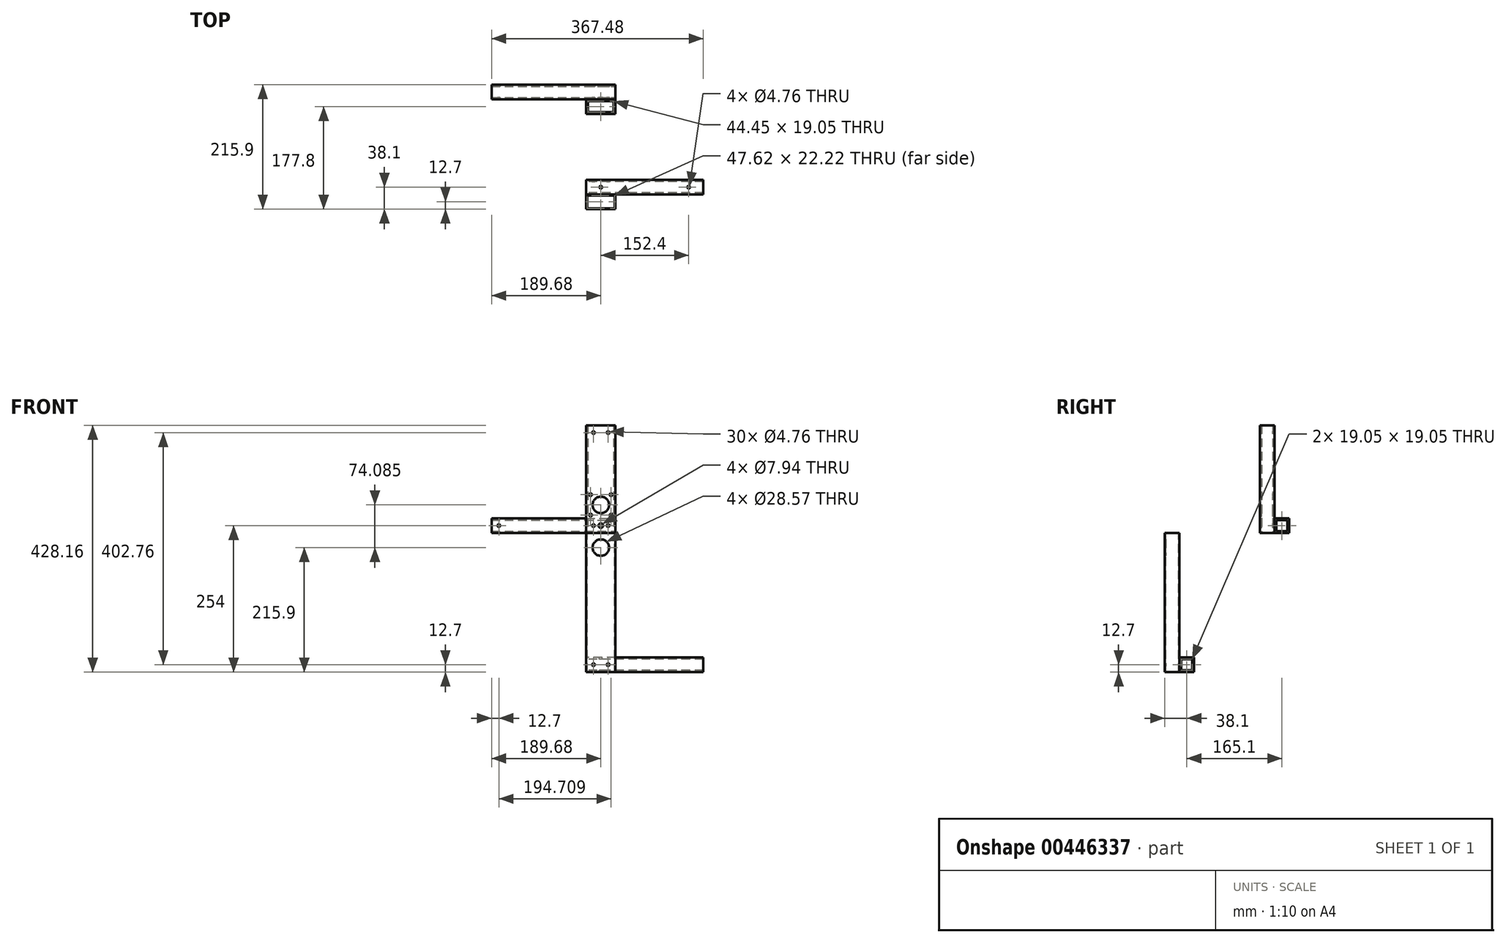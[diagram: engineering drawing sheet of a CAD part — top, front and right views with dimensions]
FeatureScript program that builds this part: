
annotation { "Feature Type Name" : "Feature", "Feature Type Description" : "" }
export const myFeature = defineFeature(function(context is Context, id is Id, definition is map)
    precondition{}
    {
        {
            var Q0;
            Q0=qCreatedBy(makeId("Top.planeOp"),FACE);
            var sketch = newSketch(context, id + "F0", { "sketchPlane" : qUnion([Q0])});
            skLineSegment(sketch, "E0.bottom", {"start": v(0, 0) * mm, "end": v(-50.8, 0) * mm});
            skLineSegment(sketch, "E0.top", {"start": v(0, -25.4) * mm, "end": v(-50.8, -25.4) * mm});
            skLineSegment(sketch, "E0.left", {"start": v(0, 0) * mm, "end": v(0, -25.4) * mm});
            skLineSegment(sketch, "E0.right", {"start": v(-50.8, 0) * mm, "end": v(-50.8, -25.4) * mm});
            skLineSegment(sketch, "E1.0", {"start": v(-3.17, -3.17) * mm, "end": v(-47.62, -3.18) * mm});
            skLineSegment(sketch, "E1.1", {"start": v(-3.17, -3.17) * mm, "end": v(-3.17, -22.22) * mm});
            skLineSegment(sketch, "E1.2", {"start": v(-3.17, -22.22) * mm, "end": v(-47.62, -22.22) * mm});
            skLineSegment(sketch, "E1.3", {"start": v(-47.62, -3.18) * mm, "end": v(-47.62, -22.22) * mm});
            skLineSegment(sketch, "E2.bottom", {"start": v(0, -165.1) * mm, "end": v(-50.8, -165.1) * mm});
            skLineSegment(sketch, "E2.top", {"start": v(0, -190.5) * mm, "end": v(-50.8, -190.5) * mm});
            skLineSegment(sketch, "E2.left", {"start": v(0, -165.1) * mm, "end": v(0, -190.5) * mm});
            skLineSegment(sketch, "E2.right", {"start": v(-50.8, -165.1) * mm, "end": v(-50.8, -190.5) * mm});
            skLineSegment(sketch, "E3.0", {"start": v(-1.59, -166.69) * mm, "end": v(-1.59, -188.91) * mm});
            skLineSegment(sketch, "E3.1", {"start": v(-1.59, -166.69) * mm, "end": v(-49.21, -166.69) * mm});
            skLineSegment(sketch, "E3.2", {"start": v(-49.21, -166.69) * mm, "end": v(-49.21, -188.91) * mm});
            skLineSegment(sketch, "E3.3", {"start": v(-1.59, -188.91) * mm, "end": v(-49.21, -188.91) * mm});
            skSolve(sketch);
        }
        {
            var Q0;
            Q0=makeQuery(id+"F0.imprint","IMPRINT",FACE,{"disambiguationData":[TD([[makeQuery(id+"F0.imprint","IMPRINT",EDGE,{"derivedFrom":sQuery(id+"F0.wireOp",EDGE,"E0.bottom")}),1.0]])]});
            extrude(context, id + "F1", {"entities" : qUnion([Q0]), "depth" : 186.86 * mm, "offsetDistance" : 25.4 * mm});
        }
        {
            var Q0;
            Q0=qCreatedBy(makeId("Right.planeOp"),FACE);
            var sketch = newSketch(context, id + "F2", { "sketchPlane" : qUnion([Q0])});
            skLineSegment(sketch, "E4.bottom", {"start": v(0, 0) * mm, "end": v(25.4, 0) * mm});
            skLineSegment(sketch, "E4.top", {"start": v(0, 25.4) * mm, "end": v(25.4, 25.4) * mm});
            skLineSegment(sketch, "E4.left", {"start": v(0, 0) * mm, "end": v(0, 25.4) * mm});
            skLineSegment(sketch, "E4.right", {"start": v(25.4, 0) * mm, "end": v(25.4, 25.4) * mm});
            skLineSegment(sketch, "E5.0", {"start": v(3.18, 22.23) * mm, "end": v(22.23, 22.23) * mm});
            skLineSegment(sketch, "E5.1", {"start": v(3.17, 3.17) * mm, "end": v(3.17, 22.23) * mm});
            skLineSegment(sketch, "E5.2", {"start": v(3.17, 3.17) * mm, "end": v(22.23, 3.17) * mm});
            skLineSegment(sketch, "E5.3", {"start": v(22.23, 3.17) * mm, "end": v(22.23, 22.22) * mm});
            skSolve(sketch);
        }
        {
            var Q0;
            Q0=makeQuery(id+"F2.imprint","IMPRINT",FACE,{"disambiguationData":[TD([[makeQuery(id+"F2.imprint","IMPRINT",EDGE,{"derivedFrom":sQuery(id+"F2.wireOp",EDGE,"E4.bottom")}),1.0]])]});
            extrude(context, id + "F3", {"entities" : qUnion([Q0]), "oppositeDirection" : true, "depth" : 215.08 * mm, "offsetDistance" : 25.4 * mm});
        }
        {
            var Q0;
            Q0=makeQuery(id+"F1.opExtrude","SWEPT_FACE",FACE,{"disambiguationData":[OSD([sQuery(id+"F0.wireOp",EDGE,"E0.bottom")])]});
            var sketch = newSketch(context, id + "F4", { "sketchPlane" : qUnion([Q0])});
            skCircle(sketch, "E6", {"center": v(25.4, 48.69) * mm, "radius": 14.29 * mm});
            skLineSegment(sketch, "E7", {"start": v(25.4, 186.86) * mm, "end": v(25.4, 0) * mm, "construction": true});
            skLineSegment(sketch, "E8.bottom", {"start": v(43.13, 66.41) * mm, "end": v(7.67, 66.41) * mm, "construction": true});
            skLineSegment(sketch, "E8.top", {"start": v(43.13, 30.96) * mm, "end": v(7.67, 30.96) * mm, "construction": true});
            skLineSegment(sketch, "E8.left", {"start": v(43.13, 66.41) * mm, "end": v(43.13, 30.96) * mm, "construction": true});
            skLineSegment(sketch, "E8.right", {"start": v(7.67, 66.41) * mm, "end": v(7.67, 30.96) * mm, "construction": true});
            skCircle(sketch, "E9", {"center": v(7.67, 66.41) * mm, "radius": 2.38 * mm});
            skCircle(sketch, "E10", {"center": v(43.13, 66.41) * mm, "radius": 2.38 * mm});
            skCircle(sketch, "E11", {"center": v(43.13, 30.96) * mm, "radius": 2.38 * mm});
            skCircle(sketch, "E12", {"center": v(7.67, 30.96) * mm, "radius": 2.38 * mm});
            skPoint(sketch, "E13", {"position": v(38.1, 12.7) * mm});
            skPoint(sketch, "E14", {"position": v(25.4, 12.7) * mm});
            skPoint(sketch, "E15", {"position": v(12.7, 12.7) * mm});
            skCircle(sketch, "E16", {"center": v(38.1, 12.7) * mm, "radius": 2.38 * mm});
            skCircle(sketch, "E17", {"center": v(25.4, 12.7) * mm, "radius": 3.97 * mm});
            skCircle(sketch, "E18", {"center": v(12.7, 12.7) * mm, "radius": 2.38 * mm});
            skLineSegment(sketch, "E19", {"start": v(50.8, 174.16) * mm, "end": v(0, 174.16) * mm, "construction": true});
            skCircle(sketch, "E20", {"center": v(38.1, 174.16) * mm, "radius": 2.38 * mm});
            skCircle(sketch, "E21", {"center": v(12.7, 174.16) * mm, "radius": 2.38 * mm});
            skLineSegment(sketch, "E22", {"start": v(215.08, 12.7) * mm, "end": v(202.38, 12.7) * mm, "construction": true});
            skCircle(sketch, "E23", {"center": v(227.78, 12.7) * mm, "radius": 2.38 * mm});
            skCircle(sketch, "E24", {"center": v(202.38, 12.7) * mm, "radius": 2.38 * mm});
            skSolve(sketch);
        }
        {
            var Q0;
            Q0 = qSketchRegion(id + "F4", true);
            extrude(context, id + "F5", {"entities" : qUnion([Q0]), "operationType" : NewBodyOperationType.REMOVE, "endBound" : BoundingType.THROUGH_ALL, "depth" : 25.4 * mm, "offsetDistance" : 25.4 * mm, "hasSecondDirection" : true, "secondDirectionOppositeDirection" : true, "secondDirectionDepth" : 25.4 * mm});
        }
        {
            var Q0;
            Q0=makeQuery(id+"F0.imprint","IMPRINT",FACE,{"disambiguationData":[TD([[makeQuery(id+"F0.imprint","IMPRINT",EDGE,{"derivedFrom":sQuery(id+"F0.wireOp",EDGE,"E2.bottom")}),1.0]])]});
            extrude(context, id + "F6", {"entities" : qUnion([Q0]), "oppositeDirection" : true, "depth" : 241.3 * mm, "offsetDistance" : 25.4 * mm});
        }
        {
            var Q0;
            Q0=makeQuery(id+"F6.opExtrude","SWEPT_FACE",FACE,{"disambiguationData":[OSD([sQuery(id+"F0.wireOp",EDGE,"E2.top")])]});
            var sketch = newSketch(context, id + "F7", { "sketchPlane" : qUnion([Q0])});
            skCircle(sketch, "E25", {"center": v(-25.4, -25.4) * mm, "radius": 14.29 * mm});
            skLineSegment(sketch, "E26", {"start": v(-25.4, 0) * mm, "end": v(-25.4, -241.3) * mm, "construction": true});
            skSolve(sketch);
        }
        {
            var Q0;
            Q0 = qSketchRegion(id + "F7", true);
            extrude(context, id + "F8", {"entities" : qUnion([Q0]), "operationType" : NewBodyOperationType.REMOVE, "endBound" : BoundingType.THROUGH_ALL, "oppositeDirection" : true, "depth" : 25.4 * mm, "offsetDistance" : 25.4 * mm});
        }
        {
            var Q0;
            Q0=makeQuery(id+"F6.opExtrude","SWEPT_FACE",FACE,{"disambiguationData":[OSD([sQuery(id+"F0.wireOp",EDGE,"E2.right")])]});
            var sketch = newSketch(context, id + "F9", { "sketchPlane" : qUnion([Q0])});
            skLineSegment(sketch, "E27.bottom", {"start": v(165.1, -241.3) * mm, "end": v(139.7, -241.3) * mm});
            skLineSegment(sketch, "E27.top", {"start": v(165.1, -215.9) * mm, "end": v(139.7, -215.9) * mm});
            skLineSegment(sketch, "E27.left", {"start": v(165.1, -241.3) * mm, "end": v(165.1, -215.9) * mm});
            skLineSegment(sketch, "E27.right", {"start": v(139.7, -241.3) * mm, "end": v(139.7, -215.9) * mm});
            skLineSegment(sketch, "E28.0", {"start": v(161.92, -219.08) * mm, "end": v(142.88, -219.08) * mm});
            skLineSegment(sketch, "E28.1", {"start": v(161.92, -238.12) * mm, "end": v(161.92, -219.08) * mm});
            skLineSegment(sketch, "E28.2", {"start": v(161.92, -238.12) * mm, "end": v(142.88, -238.12) * mm});
            skLineSegment(sketch, "E28.3", {"start": v(142.88, -238.12) * mm, "end": v(142.88, -219.08) * mm});
            skSolve(sketch);
        }
        {
            var Q0;
            Q0=makeQuery(id+"F9.imprint","IMPRINT",FACE,{"disambiguationData":[TD([[makeQuery(id+"F9.imprint","IMPRINT",EDGE,{"derivedFrom":sQuery(id+"F9.wireOp",EDGE,"E27.bottom")}),-1.0]])]});
            extrude(context, id + "F10", {"entities" : qUnion([Q0]), "oppositeDirection" : true, "depth" : 203.2 * mm, "offsetDistance" : 25.4 * mm});
        }
        {
            var Q0;
            Q0=makeQuery(id+"F6.opExtrude","SWEPT_FACE",FACE,{"disambiguationData":[OSD([sQuery(id+"F0.wireOp",EDGE,"E2.top")])]});
            var sketch = newSketch(context, id + "F11", { "sketchPlane" : qUnion([Q0])});
            skPoint(sketch, "E29", {"position": v(-38.1, -228.6) * mm});
            skPoint(sketch, "E30", {"position": v(-12.7, -228.6) * mm});
            skCircle(sketch, "E31", {"center": v(-38.1, -228.6) * mm, "radius": 2.38 * mm});
            skCircle(sketch, "E32", {"center": v(-12.7, -228.6) * mm, "radius": 2.38 * mm});
            skSolve(sketch);
        }
        {
            var Q0;
            Q0 = qSketchRegion(id + "F11", true);
            extrude(context, id + "F12", {"entities" : qUnion([Q0]), "operationType" : NewBodyOperationType.REMOVE, "endBound" : BoundingType.THROUGH_ALL, "oppositeDirection" : true, "depth" : 25.4 * mm, "offsetDistance" : 25.4 * mm});
        }
        {
            var Q0;
            Q0=makeQuery(id+"F10.opExtrude","SWEPT_FACE",FACE,{"disambiguationData":[OSD([sQuery(id+"F9.wireOp",EDGE,"E27.top")])]});
            var sketch = newSketch(context, id + "F13", { "sketchPlane" : qUnion([Q0])});
            skPoint(sketch, "E33", {"position": v(-25.4, -152.4) * mm});
            skPoint(sketch, "E34", {"position": v(127, -152.4) * mm});
            skLineSegment(sketch, "E35", {"start": v(-50.8, -152.4) * mm, "end": v(152.4, -152.4) * mm, "construction": true});
            skCircle(sketch, "E36", {"center": v(-25.4, -152.4) * mm, "radius": 2.38 * mm});
            skCircle(sketch, "E37", {"center": v(127, -152.4) * mm, "radius": 2.38 * mm});
            skSolve(sketch);
        }
        {
            var Q0;
            Q0 = qSketchRegion(id + "F13", true);
            extrude(context, id + "F14", {"entities" : qUnion([Q0]), "operationType" : NewBodyOperationType.REMOVE, "endBound" : BoundingType.THROUGH_ALL, "oppositeDirection" : true, "depth" : 25.4 * mm, "offsetDistance" : 25.4 * mm});
        }
    });
